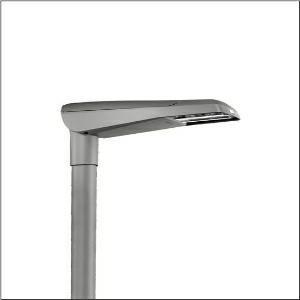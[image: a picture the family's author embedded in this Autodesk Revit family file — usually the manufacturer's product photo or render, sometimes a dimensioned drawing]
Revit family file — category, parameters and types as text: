
# Revit family: streetlight_sl_11_iq_micro___st0_5a_5xc1b41e08ce_6374
name_source: partatom
category: Lighting Fixtures
units: mm (PartAtom-declared; Revit-internal decimal feet)

## family parameters
Cut with Voids When Loaded = No
Host = Face
Light Source = No
Part Type = Normal
Room Calculation Point = No
Round Connector Dimension = Use Diameter
Shared = No

## types (1)
- --- (1 x LED, 1940 lm, 12.6 W, 4000K)
    Apparent Load = 13 VA
    CIE Flux Codes = 42 72 97 100 100
    Color Rendering = 70
    Color Temperature = 4000K
    Default Elevation = 1800 mm
    Description = Streetlight SL 11 iQ micro, mast luminaire, primary light control with 3 zone facetted reflector, of plastic, silver coated, highly specular, primary optical cover: cover, of PMMA, transparent, light distribution: ST0.5a, light emission: direct distribution, primary light characteristic: asymmetric, installation type: post-top, side-entry, lamps: LED, High Power LED, rated values: 1.940lm | 12,6W | 154lm/W (begin service life); end service life: 1.940lm | 12,9W; at 50% lumin. flux: 970lm | 6,8W | 142,6lm/W, colour temperature: 4000K, colour rendering: CRI > 70, light colour: 740, light setting 1 begin service life: 100% | 1.940lm | 12,6W | 154lm/W | 4.000K, light setting 1 end service life: 12,9W, further light settings possible, control: optimised constant luminous flux control (CLO 2.0), Desk-Remote (wireless, voltage-free reading and setting of iQ features in the workshop via application-optimized NFC function/RFID function), Light-Fading, Smart-Wire, Night-Set, Lumen-Switch, Temp-Guard, Auto-Match, with cable H07RN-F 5x 1.5mm², mains connection: 230..240V, AC, 50/60Hz, connection cable pre-assembled, cable length: 5,5m, luminaire housing, of diecast aluminium, powder-coated, Siteco® metallic grey (DB 702S), please order mast flange separately, inclination adjustable without tools: 0°, 5°, 10°, 15° (post-top) | 0°, -5°, -10°, -15° (side-entry), sealing non-destructively replaceable, multi-level sealing system, length: 600mm, width: 174mm, height: 116mm, mast flange for spigot size: 42mm (side-entry): 5XC10008XM4, 60/48mm (side-entry/post-top): 5XC10108XM2, 76/60mm (side-entry/post-top): 5XC10108XM1, equipment: standard, protection rating (complete): IP66, insulation class (complete): insulation class II (safety insulation), certification: CE, ENEC, ENEC+, VDE, impact resistance: IK10, permissible operating ambient temperature for outdoor applications: -25..+50°C, standard-compliant lighting for roads and squares, Environmental Product Declaration (EPD) tested and certified by an independent institute, packaging unit: 1 piece

Light Distribution: ST0.5a
    Height = 116 mm
    Lamp = 1 x LED
    Lamp Light Flux = 1940 lm
    Lamp Power = 12.6 W
    Lamp count = 1
    Length = 600 mm
    Luminous efficacy = 154 lm/W
    Manufacturer = Siteco
    ModVariant = No
    Model = 5XC1B41E08CE
    Number of Poles = 1
    OnlyDefault = Yes
    Power Factor = 1
    Product Name = Streetlight SL 11 iQ micro | ST0.5a
    Product group = mast luminaire | pylon top
    ProductGroupID = 6100
    Protection Class = Protection class II
    Protection Degree = IP 66
    RLX_Detail_Level = 1
    RLX_Emergency_Light_Flux = 0 lm
    RLX_Emergency_Type = 0
    RLX_Emergency_Type_DB = No
    RlxData = <blob elided: 26761 chars, md5=753f0a92>
    Socket = socket
    Standby Power = 0 W
    System Light Flux = 1940 lm
    System Power = 13 W
    Type Comments = factory setting: luminous flux: 100 % | dim-lin: 254 | 229 mA
    Type Image = l_1006566.jpg
    URL = http://relux.com
    VarID = @adj_003515
    Voltage = 0 V
    Weight = 0.00 kg
    Width = 174 mm

## geometry (parser evidence)
native form markers: Blend x4, Sweep x10
no freeform markers — native parametric forms only
